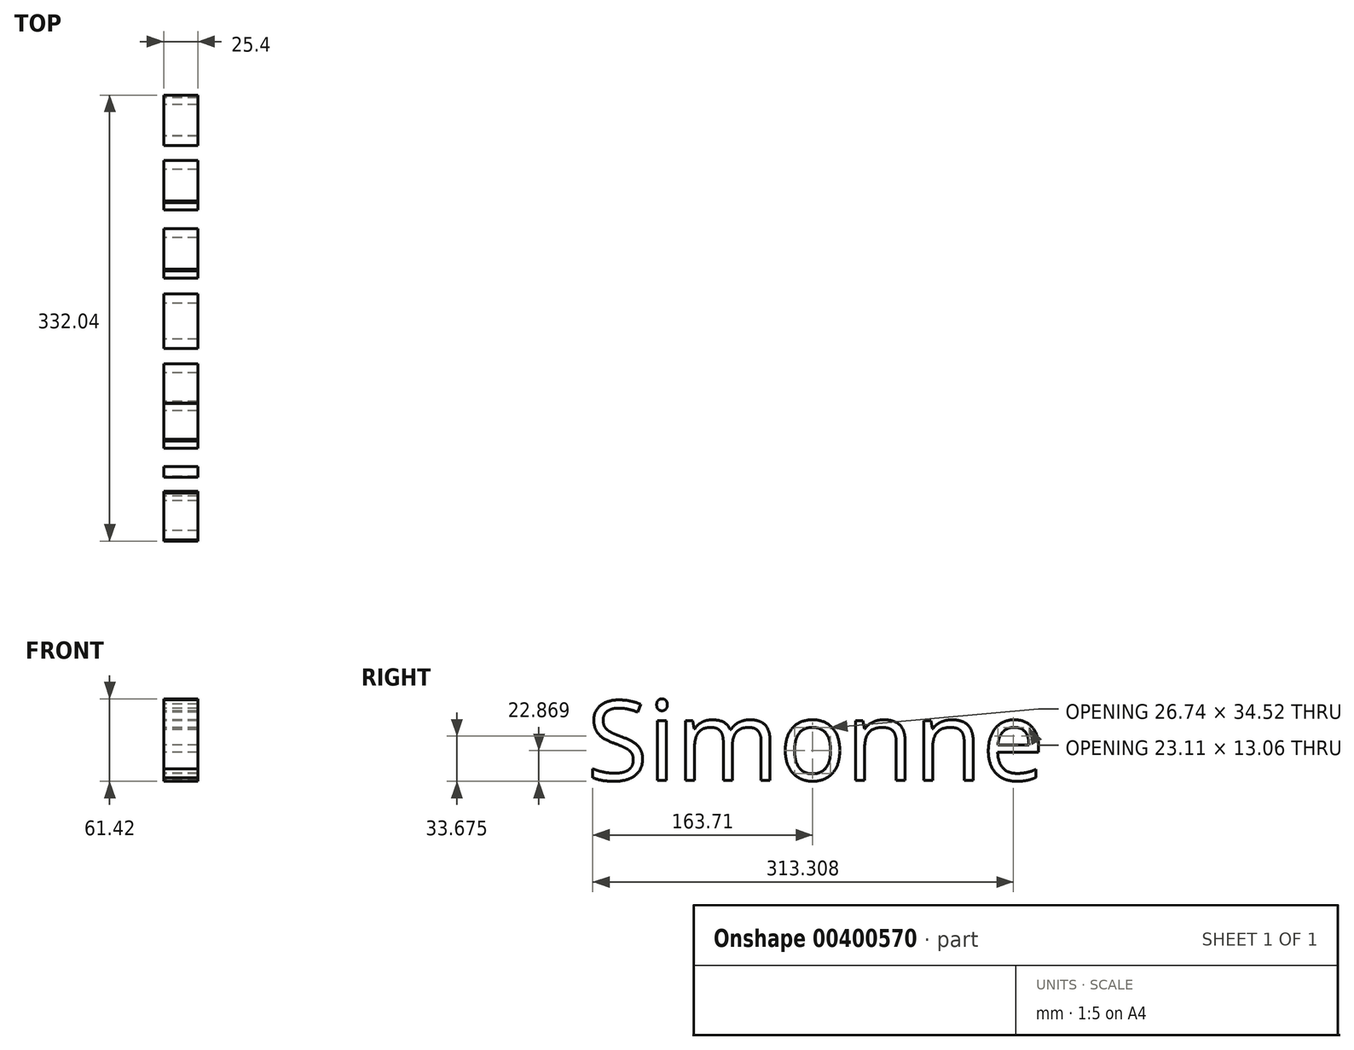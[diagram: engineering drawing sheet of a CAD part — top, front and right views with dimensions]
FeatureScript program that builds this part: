
annotation { "Feature Type Name" : "Feature", "Feature Type Description" : "" }
export const myFeature = defineFeature(function(context is Context, id is Id, definition is map)
    precondition{}
    {
        {
            var Q0;
            Q0=qCreatedBy(makeId("Right.planeOp"),FACE);
            var sketch = newSketch(context, id + "F0", { "sketchPlane" : qUnion([Q0])});
            skText(sketch, "E0", { "text": "Simonne", "fontName": "OpenSans-Regular.ttf"});
            const initialGuessF0  = {"E0": [-0.15367, -0.03207, 1, 0, 0.05946]};
            skSetInitialGuess(sketch, initialGuessF0);
            skSolve(sketch);
        }
        {
            var Q0;
            Q0 = qSketchRegion(id + "F0", true);
            extrude(context, id + "F1", {"entities" : qUnion([Q0]), "depth" : 25.4 * mm});
        }
    });
